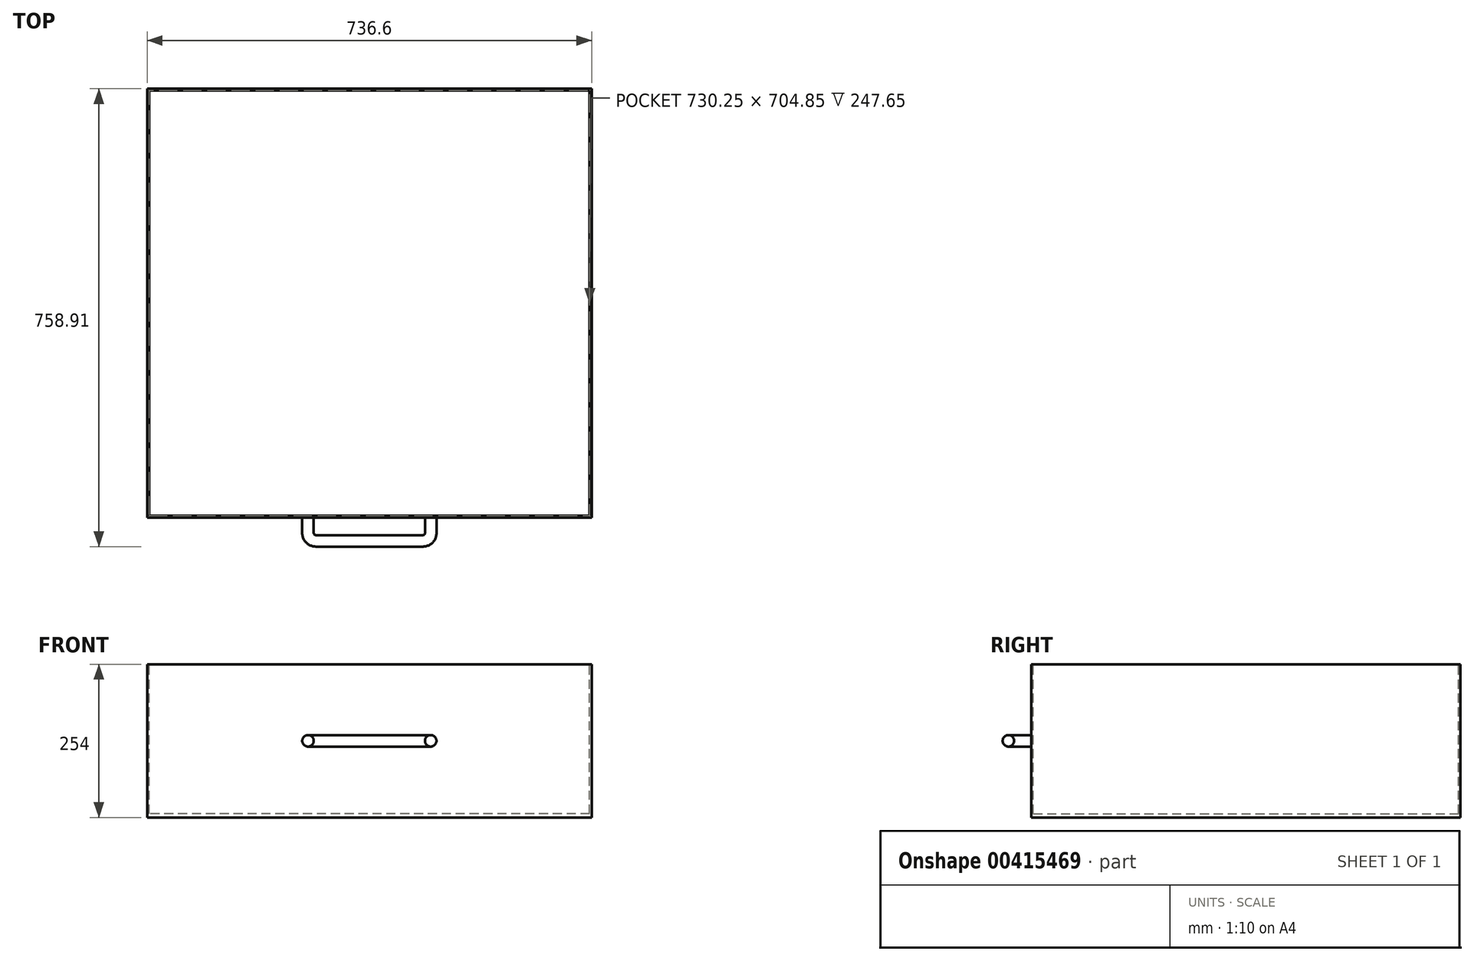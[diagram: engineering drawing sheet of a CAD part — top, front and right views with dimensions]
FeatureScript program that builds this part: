
annotation { "Feature Type Name" : "Feature", "Feature Type Description" : "" }
export const myFeature = defineFeature(function(context is Context, id is Id, definition is map)
    precondition{}
    {
        {
            var Q0;
            Q0=qCreatedBy(makeId("Front.planeOp"),FACE);
            var sketch = newSketch(context, id + "F0", { "sketchPlane" : qUnion([Q0])});
            skLineSegment(sketch, "E0.bottom", {"start": v(368.3, -127) * mm, "end": v(-368.3, -127) * mm});
            skLineSegment(sketch, "E0.top", {"start": v(368.3, 127) * mm, "end": v(-368.3, 127) * mm});
            skLineSegment(sketch, "E0.left", {"start": v(368.3, -127) * mm, "end": v(368.3, 127) * mm});
            skLineSegment(sketch, "E0.right", {"start": v(-368.3, -127) * mm, "end": v(-368.3, 127) * mm});
            skPoint(sketch, "E0.middle", {"position": v(0, 0) * mm});
            skSolve(sketch);
        }
        {
            var Q0;
            Q0=makeQuery(id+"F0.imprint","IMPRINT",FACE,{"disambiguationData":[TD([[makeQuery(id+"F0.imprint","IMPRINT",EDGE,{"derivedFrom":sQuery(id+"F0.wireOp",EDGE,"E0.bottom")}),-1.0]])]});
            extrude(context, id + "F1", {"entities" : qUnion([Q0]), "oppositeDirection" : true, "depth" : 711.2 * mm});
        }
        {
            var Q0;
            Q0=makeQuery(id+"F1.opExtrude","SWEPT_FACE",FACE,{"disambiguationData":[OSD([sQuery(id+"F0.wireOp",EDGE,"E0.top")])]});
            var sketch = newSketch(context, id + "F2", { "sketchPlane" : qUnion([Q0])});
            skLineSegment(sketch, "E1.bottom", {"start": v(365.13, 3.18) * mm, "end": v(-365.12, 3.17) * mm});
            skLineSegment(sketch, "E1.top", {"start": v(365.13, 708.03) * mm, "end": v(-365.12, 708.03) * mm});
            skLineSegment(sketch, "E1.left", {"start": v(365.13, 3.18) * mm, "end": v(365.13, 708.03) * mm});
            skLineSegment(sketch, "E1.right", {"start": v(-365.12, 3.17) * mm, "end": v(-365.12, 708.03) * mm});
            skPoint(sketch, "E1.middle", {"position": v(0, 355.6) * mm});
            skPoint(sketch, "E1.middle.positionSnap0", {"position": v(-368.3, 355.6) * mm});
            skPoint(sketch, "E1.centerSnap0", {"position": v(-368.3, 355.6) * mm});
            skSolve(sketch);
        }
        {
            var Q0;
            Q0=makeQuery(id+"F2.imprint","IMPRINT",FACE,{"disambiguationData":[TD([[makeQuery(id+"F2.imprint","IMPRINT",EDGE,{"derivedFrom":sQuery(id+"F2.wireOp",EDGE,"E1.bottom")}),-1.0]])]});
            extrude(context, id + "F3", {"entities" : qUnion([Q0]), "operationType" : NewBodyOperationType.REMOVE, "oppositeDirection" : true, "depth" : 247.65 * mm});
        }
        {
            var Q0;
            Q0=qCreatedBy(makeId("Top.planeOp"),FACE);
            var sketch = newSketch(context, id + "F4", { "sketchPlane" : qUnion([Q0])});
            skLineSegment(sketch, "E2", {"start": v(-101.6, 0) * mm, "end": v(-101.6, -25.4) * mm});
            skLineSegment(sketch, "E3", {"start": v(-101.6, -25.4) * mm, "end": v(-88.9, -25.4) * mm});
            skLineSegment(sketch, "E4", {"start": v(-88.9, -25.4) * mm, "end": v(-88.9, -38.1) * mm});
            skLineSegment(sketch, "E5", {"start": v(-88.9, -38.1) * mm, "end": v(88.9, -38.1) * mm});
            skLineSegment(sketch, "E6", {"start": v(88.9, -38.1) * mm, "end": v(88.9, -25.4) * mm});
            skLineSegment(sketch, "E7", {"start": v(88.9, -25.4) * mm, "end": v(101.6, -25.4) * mm});
            skLineSegment(sketch, "E8", {"start": v(101.6, -25.4) * mm, "end": v(101.6, 0) * mm});
            skArc(sketch, "E9", {"start": v(-88.9, -38.1) * mm, "mid": v(-97.88, -34.38) * mm, "end": v(-101.6, -25.4) * mm});
            skArc(sketch, "E10", {"start": v(88.9, -38.1) * mm, "mid": v(97.88, -34.38) * mm, "end": v(101.6, -25.4) * mm});
            skSolve(sketch);
        }
        {
            var Q0;
            Q0=makeQuery(id+"F1.opExtrude","CAP_FACE",FACE,{"disambiguationData":[OSD([sQuery(id+"F0.wireOp",EDGE,"E0.bottom"),sQuery(id+"F0.wireOp",EDGE,"E0.top"),sQuery(id+"F0.wireOp",EDGE,"E0.left"),sQuery(id+"F0.wireOp",EDGE,"E0.right")])],"isStart":true});
            var sketch = newSketch(context, id + "F5", { "sketchPlane" : qUnion([Q0])});
            skCircle(sketch, "E11", {"center": v(-101.68, 0) * mm, "radius": 9.53 * mm});
            skSolve(sketch);
        }
        {
            var Q0;
            Q0=makeQuery(id+"F5.imprint","IMPRINT",FACE,{"disambiguationData":[TD([[makeQuery(id+"F5.imprint","IMPRINT",EDGE,{"derivedFrom":sQuery(id+"F5.wireOp",EDGE,"E11")}),1.0]])]});
            var Q1;
            Q1=sQuery(id+"F4.wireOp",EDGE,"E2");
            var Q2;
            Q2=sQuery(id+"F4.wireOp",EDGE,"E9");
            var Q3;
            Q3=sQuery(id+"F4.wireOp",EDGE,"E5");
            var Q4;
            Q4=sQuery(id+"F4.wireOp",EDGE,"E10");
            var Q5;
            Q5=sQuery(id+"F4.wireOp",EDGE,"E8");
            sweep(context, id + "F6", {"operationType" : NewBodyOperationType.ADD, "profiles" : qUnion([Q0]), "path" : qUnion([Q1, Q2, Q3, Q4, Q5])});
        }
    });
